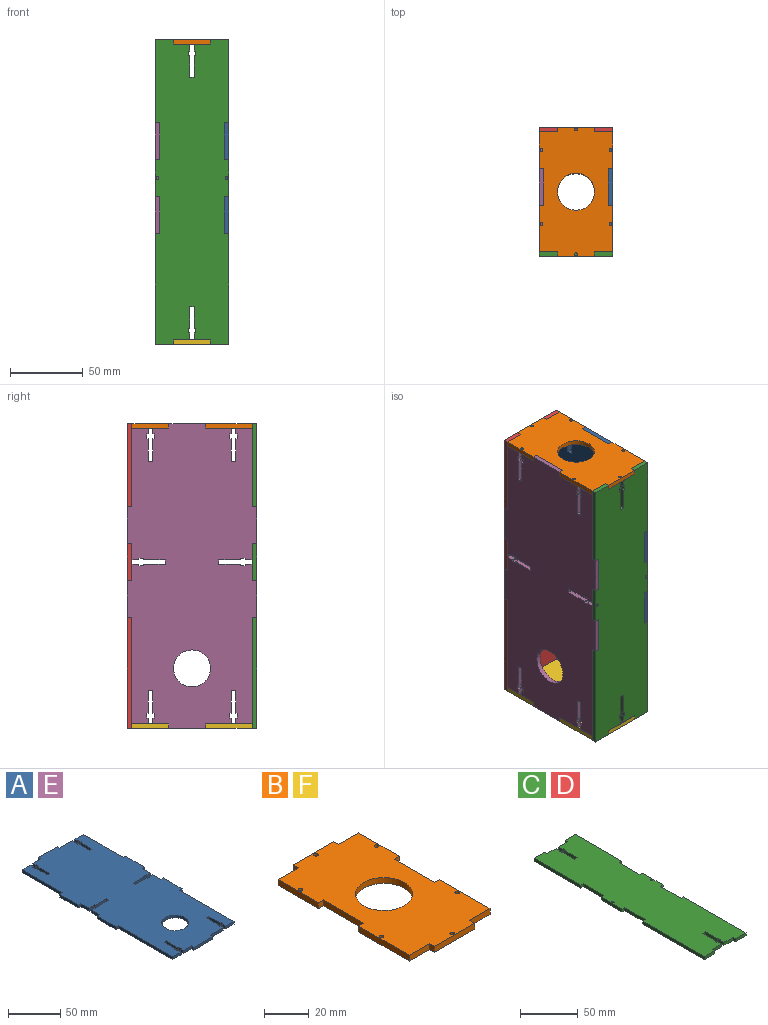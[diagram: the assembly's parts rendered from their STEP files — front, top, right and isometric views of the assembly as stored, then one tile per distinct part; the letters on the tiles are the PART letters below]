
ASSEMBLY  parts=6 mates=5
PART A: 103 faces, bbox 88.9x209.6x3.2 mm
  f0: plane 11.2x3.18mm, normal (0,-1,0), area 35.6mm2, adj f1,f100,f101,f102
  f1: plane 3.98x3.18mm, normal (1,0,0), area 12.6mm2, adj f0,f2,f101,f102
  f2: plane 3.18x1.04mm, normal (0,1,0), area 3.3mm2, adj f1,f3,f101,f102
  f3: plane 3.18x3.18mm, normal (1,0,0), area 10.1mm2, adj f2,f4,f101,f102
  f4: plane 3.18x1.04mm, normal (0,-1,0), area 3.3mm2, adj f3,f5,f101,f102
  f5: plane 15.7x3.18mm, normal (1,0,0), area 49.9mm2, adj f4,f6,f101,f102
  f6: plane 3.18x3mm, normal (0,-1,0), area 9.5mm2, adj f5,f7,f101,f102
  f7: plane 15.7x3.18mm, normal (-1,0,0), area 49.9mm2, adj f6,f8,f101,f102
  f8: plane 3.18x1.04mm, normal (0,-1,0), area 3.3mm2, adj f7,f9,f101,f102
  f9: plane 3.18x3.18mm, normal (-1,0,0), area 10.1mm2, adj f8,f10,f101,f102
  f10: plane 3.18x1.04mm, normal (0,1,0), area 3.3mm2, adj f9,f11,f101,f102
  f11: plane 3.98x3.18mm, normal (-1,0,0), area 12.6mm2, adj f10,f12,f101,f102
  f12: plane 11.2x3.18mm, normal (0,-1,0), area 35.6mm2, adj f11,f13,f101,f102
  f13: plane 3.18x3.18mm, normal (-1,0,0), area 10.1mm2, adj f12,f14,f101,f102
  f14: plane 25.4x3.18mm, normal (0,-1,0), area 80.6mm2, adj f13,f15,f101,f102
  f15: plane 3.18x3.18mm, normal (1,0,0), area 10.1mm2, adj f14,f16,f101,f102
  f16: plane 17.55x3.18mm, normal (0,-1,0), area 55.7mm2, adj f15,f17,f101,f102
  f17: plane 3.98x3.18mm, normal (1,0,0), area 12.6mm2, adj f16,f18,f101,f102
  f18: plane 3.18x1.04mm, normal (0,1,0), area 3.3mm2, adj f17,f19,f101,f102
  f19: plane 3.18x3.18mm, normal (1,0,0), area 10.1mm2, adj f18,f20,f101,f102
  f20: plane 3.18x1.04mm, normal (0,-1,0), area 3.3mm2, adj f19,f21,f101,f102
  f21: plane 15.7x3.18mm, normal (1,0,0), area 49.9mm2, adj f20,f22,f101,f102
  f22: plane 3.18x3mm, normal (0,-1,0), area 9.5mm2, adj f21,f23,f101,f102
  f23: plane 15.7x3.18mm, normal (-1,0,0), area 49.9mm2, adj f22,f24,f101,f102
  f24: plane 3.18x1.04mm, normal (0,-1,0), area 3.3mm2, adj f23,f25,f101,f102
  f25: plane 3.18x3.18mm, normal (-1,0,0), area 10.1mm2, adj f24,f26,f101,f102
  f26: plane 3.18x1.04mm, normal (0,1,0), area 3.3mm2, adj f25,f27,f101,f102
  f27: plane 3.98x3.18mm, normal (-1,0,0), area 12.6mm2, adj f26,f28,f101,f102
  f28: plane 11.2x3.18mm, normal (0,-1,0), area 35.6mm2, adj f27,f29,f101,f102
  f29: plane 73.03x3.18mm, normal (1,0,0), area 231.9mm2, adj f28,f30,f101,f102
  f30: plane 3.18x3.18mm, normal (0,-1,0), area 10.1mm2, adj f29,f31,f101,f102
  f31: plane 25.4x3.18mm, normal (1,0,0), area 80.6mm2, adj f30,f32,f101,f102
  f32: plane 3.18x3.18mm, normal (0,1,0), area 10.1mm2, adj f31,f33,f101,f102
  f33: plane 11.2x3.18mm, normal (1,0,0), area 35.6mm2, adj f32,f34,f101,f102
  f34: plane 4.76x3.18mm, normal (0,1,0), area 15.1mm2, adj f33,f35,f101,f102
  f35: plane 3.18x1.04mm, normal (-1,0,0), area 3.3mm2, adj f34,f36,f101,f102
  f36: plane 3.18x3.18mm, normal (0,1,0), area 10.1mm2, adj f35,f37,f101,f102
  f37: plane 3.18x1.04mm, normal (1,0,0), area 3.3mm2, adj f36,f38,f101,f102
  f38: plane 14.95x3.18mm, normal (0,1,0), area 47.5mm2, adj f37,f39,f101,f102
  f39: plane 3.18x3mm, normal (1,-0.01,0), area 9.5mm2, adj f38,f40,f101,f102
  f40: plane 14.92x3.18mm, normal (0,-1,0), area 47.4mm2, adj f39,f41,f101,f102
  f41: plane 3.18x1.04mm, normal (1,0,0), area 3.3mm2, adj f40,f42,f101,f102
  f42: plane 3.18x3.18mm, normal (0,-1,0), area 10.1mm2, adj f41,f43,f101,f102
  f43: plane 3.18x1.04mm, normal (-1,0,0), area 3.3mm2, adj f42,f44,f101,f102
  f44: plane 4.76x3.18mm, normal (0,-1,0), area 15.1mm2, adj f43,f45,f101,f102
  f45: plane 11.2x3.18mm, normal (1,0,0), area 35.6mm2, adj f44,f46,f101,f102
  f46: plane 3.18x3.18mm, normal (0,-1,0), area 10.1mm2, adj f45,f47,f101,f102
  f47: plane 25.4x3.18mm, normal (1,0,0), area 80.6mm2, adj f46,f48,f101,f102
  f48: plane 3.18x3.18mm, normal (0,1,0), area 10.1mm2, adj f47,f49,f101,f102
  f49: plane 53.98x3.18mm, normal (1,0,0), area 171.4mm2, adj f48,f50,f101,f102
  f50: plane 11.2x3.18mm, normal (0,1,0), area 35.6mm2, adj f49,f51,f101,f102
  f51: plane 3.98x3.18mm, normal (-1,0,0), area 12.6mm2, adj f50,f52,f101,f102
  f52: plane 3.18x1.04mm, normal (0,-1,0), area 3.3mm2, adj f51,f53,f101,f102
  f53: plane 3.18x3.18mm, normal (-1,0,0), area 10.1mm2, adj f52,f54,f101,f102
  f54: plane 3.18x1.04mm, normal (0,1,0), area 3.3mm2, adj f53,f55,f101,f102
  f55: plane 15.7x3.18mm, normal (-1,0,0), area 49.9mm2, adj f54,f56,f101,f102
  f56: plane 3.18x3mm, normal (0,1,0), area 9.5mm2, adj f55,f57,f101,f102
  f57: plane 15.7x3.18mm, normal (1,0,0), area 49.9mm2, adj f56,f58,f101,f102
  f58: plane 3.18x1.04mm, normal (0,1,0), area 3.3mm2, adj f57,f59,f101,f102
  f59: plane 3.18x3.18mm, normal (1,0,0), area 10.1mm2, adj f58,f60,f101,f102
  f60: plane 3.18x1.04mm, normal (0,-1,0), area 3.3mm2, adj f59,f61,f101,f102
  f61: plane 3.98x3.18mm, normal (1,0,0), area 12.6mm2, adj f60,f62,f101,f102
  f62: plane 17.55x3.18mm, normal (0,1,0), area 55.7mm2, adj f61,f63,f101,f102
  f63: plane 3.18x3.18mm, normal (1,0,0), area 10.1mm2, adj f62,f64,f101,f102
  f64: plane 25.4x3.18mm, normal (0,1,0), area 80.6mm2, adj f63,f65,f101,f102
  f65: plane 3.18x3.18mm, normal (-1,0,0), area 10.1mm2, adj f64,f66,f101,f102
  f66: plane 11.2x3.18mm, normal (0,1,0), area 35.6mm2, adj f65,f67,f101,f102
  f67: plane 3.98x3.18mm, normal (-1,0,0), area 12.6mm2, adj f66,f68,f101,f102
  f68: plane 3.18x1.04mm, normal (0,-1,0), area 3.3mm2, adj f67,f69,f101,f102
  f69: plane 3.18x3.18mm, normal (-1,0,0), area 10.1mm2, adj f68,f70,f101,f102
  f70: plane 3.18x1.04mm, normal (0,1,0), area 3.3mm2, adj f69,f71,f101,f102
  f71: plane 15.7x3.18mm, normal (-1,0,0), area 49.9mm2, adj f70,f72,f101,f102
  f72: plane 3.18x3mm, normal (0,1,0), area 9.5mm2, adj f71,f73,f101,f102
  f73: plane 15.7x3.18mm, normal (1,0,0), area 49.9mm2, adj f72,f74,f101,f102
  f74: plane 3.18x1.04mm, normal (0,1,0), area 3.3mm2, adj f73,f75,f101,f102
  f75: plane 3.18x3.18mm, normal (1,0,0), area 10.1mm2, adj f74,f76,f101,f102
  f76: plane 3.18x1.04mm, normal (0,-1,0), area 3.3mm2, adj f75,f77,f101,f102
  f77: plane 3.98x3.18mm, normal (1,0,0), area 12.6mm2, adj f76,f78,f101,f102
  f78: plane 11.2x3.18mm, normal (0,1,0), area 35.6mm2, adj f77,f79,f101,f102
  f79: plane 53.98x3.18mm, normal (-1,0,0), area 171.4mm2, adj f78,f80,f101,f102
  f80: plane 3.18x3.18mm, normal (0,1,0), area 10.1mm2, adj f79,f81,f101,f102
  f81: plane 25.4x3.18mm, normal (-1,0,0), area 80.6mm2, adj f80,f82,f101,f102
  f82: plane 3.18x3.18mm, normal (0,-1,0), area 10.1mm2, adj f81,f83,f101,f102
  f83: plane 11.2x3.18mm, normal (-1,0,0), area 35.6mm2, adj f82,f84,f101,f102
  f84: plane 4.76x3.18mm, normal (0,-1,0), area 15.1mm2, adj f83,f85,f101,f102
  f85: plane 3.18x1.04mm, normal (1,0,0), area 3.3mm2, adj f84,f86,f101,f102
  f86: plane 3.18x3.18mm, normal (0,-1,0), area 10.1mm2, adj f85,f87,f101,f102
  f87: plane 3.18x1.04mm, normal (-1,0,0), area 3.3mm2, adj f86,f88,f101,f102
  f88: plane 14.92x3.18mm, normal (0,-1,0), area 47.4mm2, adj f87,f89,f101,f102
  f89: plane 3.18x3mm, normal (-1,-0.01,0), area 9.5mm2, adj f88,f90,f101,f102
  f90: plane 14.95x3.18mm, normal (0,1,0), area 47.5mm2, adj f89,f91,f101,f102
  f91: plane 3.18x1.04mm, normal (-1,0,0), area 3.3mm2, adj f90,f92,f101,f102
  f92: plane 3.18x3.18mm, normal (0,1,0), area 10.1mm2, adj f91,f93,f101,f102
  f93: plane 3.18x1.04mm, normal (1,0,0), area 3.3mm2, adj f92,f94,f101,f102
  f94: plane 4.76x3.18mm, normal (0,1,0), area 15.1mm2, adj f93,f95,f101,f102
  f95: plane 11.2x3.18mm, normal (-1,0,0), area 35.6mm2, adj f94,f96,f101,f102
  f96: plane 3.18x3.18mm, normal (0,1,0), area 10.1mm2, adj f95,f97,f101,f102
  f97: plane 25.4x3.18mm, normal (-1,0,0), area 80.6mm2, adj f96,f98,f101,f102
  f98: plane 3.18x3.18mm, normal (0,-1,0), area 10.1mm2, adj f97,f100,f101,f102
  f99: cylinder r=12.7mm len=25.4mm, axis (0,0,-1), area 253.4mm2, adj f101,f102
  f100: plane 73.03x3.18mm, normal (-1,0,0), area 231.9mm2, adj f0,f98,f101,f102
  f101: plane 209.55x88.9mm, normal (0,0,1), area 16300.1mm2, adj f0,f1,f2,f3,f4,f5,f6,f7
  f102: plane 209.55x88.9mm, normal (0,0,-1), area 16300.1mm2, adj f0,f1,f2,f3,f4,f5,f6,f7
PART B: 29 faces, bbox 50.8x88.9x3.2 mm
  f0: plane 12.7x3.18mm, normal (0,-1,0), area 40.3mm2, adj f1,f26,f27,f28
  f1: plane 31.75x3.18mm, normal (1,0,0), area 100.8mm2, adj f0,f2,f27,f28
  f2: plane 3.18x3.18mm, normal (0,1,0), area 10.1mm2, adj f1,f3,f27,f28
  f3: plane 25.4x3.18mm, normal (1,0,0), area 80.6mm2, adj f2,f4,f27,f28
  f4: plane 3.18x3.18mm, normal (0,-1,0), area 10.1mm2, adj f3,f5,f27,f28
  f5: plane 25.4x3.18mm, normal (1,0,0), area 80.6mm2, adj f4,f6,f27,f28
  f6: plane 12.7x3.18mm, normal (0,1,0), area 40.3mm2, adj f5,f7,f27,f28
  f7: plane 3.18x3.18mm, normal (1,0,0), area 10.1mm2, adj f6,f8,f27,f28
  f8: plane 25.4x3.18mm, normal (0,1,0), area 80.6mm2, adj f7,f9,f27,f28
  f9: plane 3.18x3.18mm, normal (-1,0,0), area 10.1mm2, adj f8,f10,f27,f28
  f10: plane 12.7x3.18mm, normal (0,1,0), area 40.3mm2, adj f9,f11,f27,f28
  f11: plane 25.4x3.18mm, normal (-1,0,0), area 80.6mm2, adj f10,f12,f27,f28
  f12: plane 3.18x3.18mm, normal (0,-1,0), area 10.1mm2, adj f11,f13,f27,f28
  f13: plane 25.4x3.18mm, normal (-1,0,0), area 80.6mm2, adj f12,f14,f27,f28
  f14: plane 3.18x3.18mm, normal (0,1,0), area 10.1mm2, adj f13,f15,f27,f28
  f15: plane 31.75x3.18mm, normal (-1,0,0), area 100.8mm2, adj f14,f16,f27,f28
  f16: plane 12.7x3.18mm, normal (0,-1,0), area 40.3mm2, adj f15,f17,f27,f28
  f17: plane 3.18x3.18mm, normal (-1,0,0), area 10.1mm2, adj f16,f18,f27,f28
  f18: plane 25.4x3.18mm, normal (0,-1,0), area 80.6mm2, adj f17,f26,f27,f28
  f19: cylinder r=1mm len=3.18mm, axis (0,0,-1), area 19.9mm2, adj f27,f28
  f20: cylinder r=1mm len=3.18mm, axis (0,0,-1), area 19.9mm2, adj f27,f28
  f21: cylinder r=1mm len=3.18mm, axis (0,0,-1), area 19.9mm2, adj f27,f28
  f22: cylinder r=1mm len=3.18mm, axis (0,0,-1), area 19.9mm2, adj f27,f28
  f23: cylinder r=1mm len=3.18mm, axis (0,0,-1), area 19.9mm2, adj f27,f28
  f24: cylinder r=1mm len=3.18mm, axis (0,0,-1), area 19.9mm2, adj f27,f28
  f25: cylinder r=12.7mm len=25.4mm, axis (0,0,-1), area 253.4mm2, adj f27,f28
  f26: plane 3.18x3.18mm, normal (1,0,0), area 10.1mm2, adj f0,f18,f27,f28
  f27: plane 88.9x50.8mm, normal (0,0,1), area 3668mm2, adj f0,f1,f2,f3,f4,f5,f6,f7
  f28: plane 88.9x50.8mm, normal (0,0,-1), area 3668mm2, adj f0,f1,f2,f3,f4,f5,f6,f7
PART C: 56 faces, bbox 50.8x209.6x3.2 mm
  f0: plane 4.76x3.18mm, normal (-1,0,0), area 15.1mm2, adj f1,f53,f54,f55
  f1: plane 3.18x1.04mm, normal (0,-1,0), area 3.3mm2, adj f0,f2,f54,f55
  f2: plane 3.18x3.18mm, normal (-1,0,0), area 10.1mm2, adj f1,f3,f54,f55
  f3: plane 3.18x1.04mm, normal (0,1,0), area 3.3mm2, adj f2,f4,f54,f55
  f4: plane 14.92x3.18mm, normal (-1,0,0), area 47.4mm2, adj f3,f5,f54,f55
  f5: plane 3.18x3mm, normal (-0.02,1,0), area 9.5mm2, adj f4,f6,f54,f55
  f6: plane 14.97x3.18mm, normal (1,0,0), area 47.5mm2, adj f5,f7,f54,f55
  f7: plane 3.18x1.04mm, normal (0,1,0), area 3.3mm2, adj f6,f8,f54,f55
  f8: plane 3.18x3.18mm, normal (1,0,0), area 10.1mm2, adj f7,f9,f54,f55
  f9: plane 3.18x1.04mm, normal (0,-1,0), area 3.3mm2, adj f8,f10,f54,f55
  f10: plane 4.76x3.18mm, normal (1,0,0), area 15.1mm2, adj f9,f11,f54,f55
  f11: plane 11.2x3.18mm, normal (0,1,0), area 35.6mm2, adj f10,f12,f54,f55
  f12: plane 3.18x3.18mm, normal (1,0,0), area 10.1mm2, adj f11,f13,f54,f55
  f13: plane 12.7x3.18mm, normal (0,1,0), area 40.3mm2, adj f12,f14,f54,f55
  f14: plane 57.15x3.18mm, normal (-1,0,0), area 181.5mm2, adj f13,f15,f54,f55
  f15: plane 3.18x3.18mm, normal (0,-1,0), area 10.1mm2, adj f14,f16,f54,f55
  f16: plane 25.4x3.18mm, normal (-1,0,0), area 80.6mm2, adj f15,f17,f54,f55
  f17: plane 3.18x3.18mm, normal (0,1,0), area 10.1mm2, adj f16,f18,f54,f55
  f18: plane 25.4x3.18mm, normal (-1,0,0), area 80.6mm2, adj f17,f19,f54,f55
  f19: plane 3.18x3.18mm, normal (0,-1,0), area 10.1mm2, adj f18,f20,f54,f55
  f20: plane 25.4x3.18mm, normal (-1,0,0), area 80.6mm2, adj f19,f21,f54,f55
  f21: plane 3.18x3.18mm, normal (0,1,0), area 10.1mm2, adj f20,f22,f54,f55
  f22: plane 76.2x3.18mm, normal (-1,0,0), area 241.9mm2, adj f21,f23,f54,f55
  f23: plane 12.7x3.18mm, normal (0,-1,0), area 40.3mm2, adj f22,f24,f54,f55
  f24: plane 3.18x3.18mm, normal (1,0,0), area 10.1mm2, adj f23,f25,f54,f55
  f25: plane 11.2x3.18mm, normal (0,-1,0), area 35.6mm2, adj f24,f26,f54,f55
  f26: plane 4.76x3.18mm, normal (1,0,0), area 15.1mm2, adj f25,f27,f54,f55
  f27: plane 3.18x1.04mm, normal (0,1,0), area 3.3mm2, adj f26,f28,f54,f55
  f28: plane 3.18x3.18mm, normal (1,0,0), area 10.1mm2, adj f27,f29,f54,f55
  f29: plane 3.18x1.04mm, normal (0,-1,0), area 3.3mm2, adj f28,f30,f54,f55
  f30: plane 14.97x3.18mm, normal (1,0,0), area 47.5mm2, adj f29,f31,f54,f55
  f31: plane 3.18x3mm, normal (-0.02,-1,0), area 9.5mm2, adj f30,f32,f54,f55
  f32: plane 14.92x3.18mm, normal (-1,0,0), area 47.4mm2, adj f31,f33,f54,f55
  f33: plane 3.18x1.04mm, normal (0,-1,0), area 3.3mm2, adj f32,f34,f54,f55
  f34: plane 3.18x3.18mm, normal (-1,0,0), area 10.1mm2, adj f33,f35,f54,f55
  f35: plane 3.18x1.04mm, normal (0,1,0), area 3.3mm2, adj f34,f36,f54,f55
  f36: plane 4.76x3.18mm, normal (-1,0,0), area 15.1mm2, adj f35,f37,f54,f55
  f37: plane 11.2x3.18mm, normal (0,-1,0), area 35.6mm2, adj f36,f38,f54,f55
  f38: plane 3.18x3.18mm, normal (-1,0,0), area 10.1mm2, adj f37,f39,f54,f55
  f39: plane 12.7x3.18mm, normal (0,-1,0), area 40.3mm2, adj f38,f40,f54,f55
  f40: plane 76.2x3.18mm, normal (1,0,0), area 241.9mm2, adj f39,f41,f54,f55
  f41: plane 3.18x3.18mm, normal (0,1,0), area 10.1mm2, adj f40,f42,f54,f55
  f42: plane 25.4x3.18mm, normal (1,0,0), area 80.6mm2, adj f41,f43,f54,f55
  f43: plane 3.18x3.18mm, normal (0,-1,0), area 10.1mm2, adj f42,f44,f54,f55
  f44: plane 25.4x3.18mm, normal (1,0,0), area 80.6mm2, adj f43,f45,f54,f55
  f45: plane 3.18x3.18mm, normal (0,1,0), area 10.1mm2, adj f44,f46,f54,f55
  f46: plane 25.4x3.18mm, normal (1,0,0), area 80.6mm2, adj f45,f47,f54,f55
  f47: plane 3.18x3.18mm, normal (0,-1,0), area 10.1mm2, adj f46,f48,f54,f55
  f48: plane 57.15x3.18mm, normal (1,0,0), area 181.5mm2, adj f47,f49,f54,f55
  f49: plane 12.7x3.18mm, normal (0,1,0), area 40.3mm2, adj f48,f50,f54,f55
  f50: plane 3.18x3.18mm, normal (-1,0,0), area 10.1mm2, adj f49,f53,f54,f55
  f51: cylinder r=1mm len=3.18mm, axis (0,0,-1), area 19.9mm2, adj f54,f55
  f52: cylinder r=1mm len=3.18mm, axis (0,0,-1), area 19.9mm2, adj f54,f55
  f53: plane 11.2x3.18mm, normal (0,1,0), area 35.6mm2, adj f0,f50,f54,f55
  f54: plane 209.55x50.8mm, normal (0,0,1), area 10004.5mm2, adj f0,f1,f2,f3,f4,f5,f6,f7
  f55: plane 209.55x50.8mm, normal (0,0,-1), area 10004.5mm2, adj f0,f1,f2,f3,f4,f5,f6,f7
PART D: same geometry as C
PART E: same geometry as A
PART F: same geometry as B
PLACE A rot(axis=(0.58,-0.58,-0.58),120deg) t=(9.17,89.81,-142.13)mm
PLACE B t=(-16.23,11.61,-40.53)mm
PLACE C rot(axis=(1,0,0),90deg) t=(53.46,-29.66,-142.13)mm
PLACE D rot(axis=(1,0,0),90deg) t=(53.46,56.06,-142.13)mm
PLACE E rot(axis=(0.58,-0.58,-0.58),120deg) t=(-38.45,89.81,-142.13)mm
PLACE F rot(axis=(0,-1,0),180deg) t=(-16.23,11.61,-243.73)mm
MATE planar C.f50 <-> B.f26  axis (-1,0,0) through (-3.53,-31.25,-38.94)mm
MATE planar E.f63 <-> B.f14  axis (0,-1,0) through (-40.04,2.09,-38.94)mm
MATE planar D.f50 <-> B.f7  axis (-1,0,0) through (-3.53,54.47,-38.94)mm
MATE planar F.f12 <-> A.f13  axis (0,-1,0) through (7.58,27.49,-245.32)mm
MATE planar A.f63 <-> B.f2  axis (0,-1,0) through (7.58,2.09,-38.94)mm
